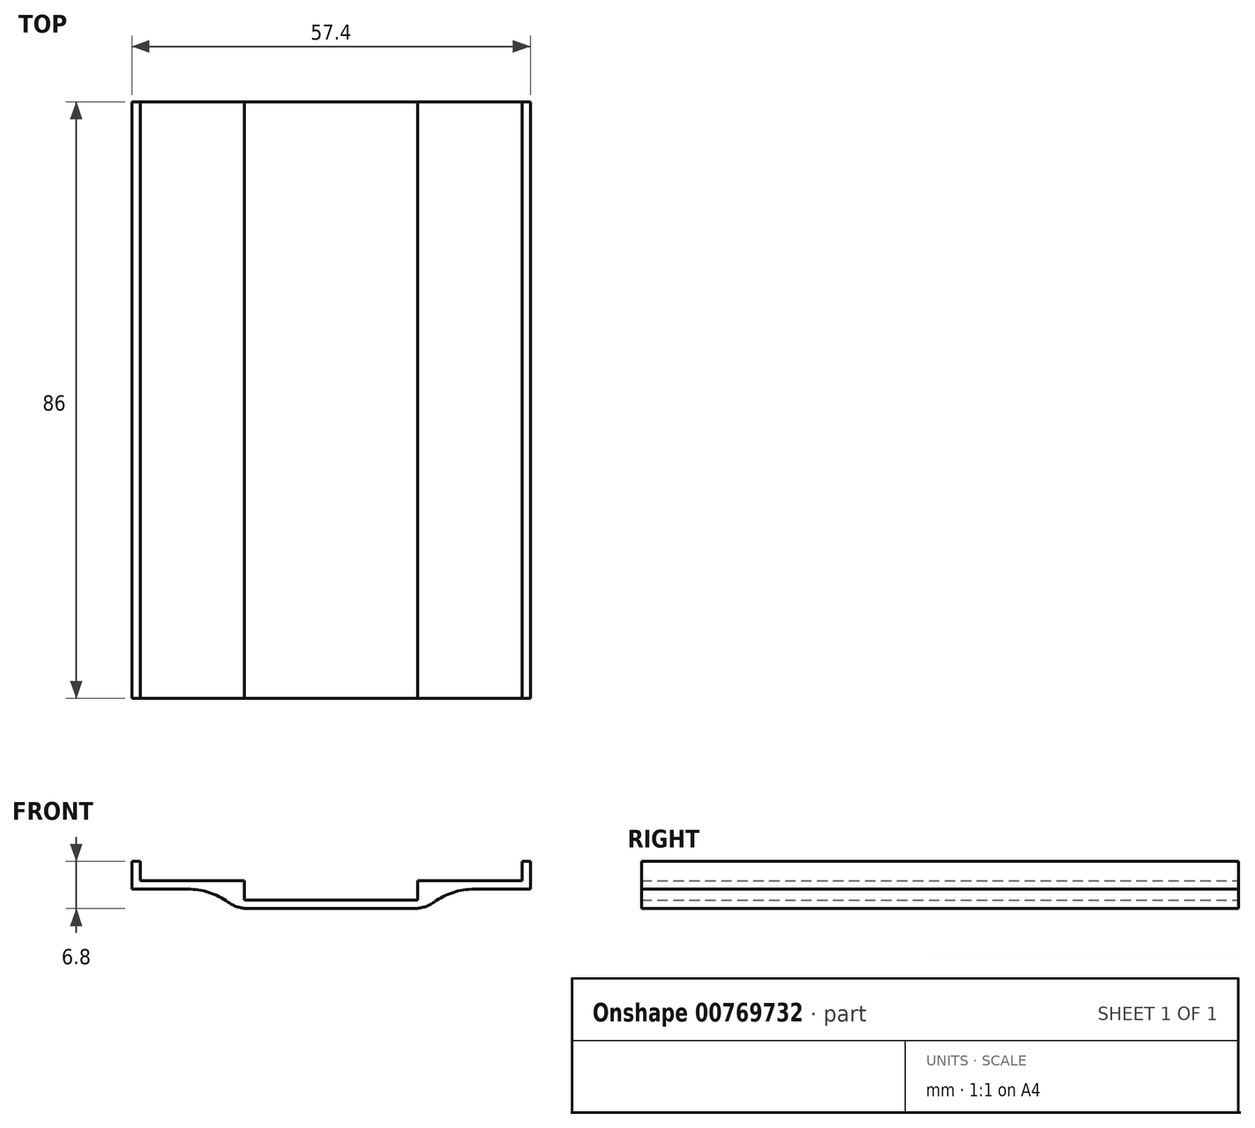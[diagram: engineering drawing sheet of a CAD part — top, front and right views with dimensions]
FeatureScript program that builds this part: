
annotation { "Feature Type Name" : "Feature", "Feature Type Description" : "" }
export const myFeature = defineFeature(function(context is Context, id is Id, definition is map)
    precondition{}
    {
        {
            var Q0;
            Q0=qCreatedBy(makeId("Front.planeOp"),FACE);
            var sketch = newSketch(context, id + "F0", { "sketchPlane" : qUnion([Q0])});
            skLineSegment(sketch, "E0.bottom", {"start": v(-27.5, 2.8) * mm, "end": v(-12.5, 2.8) * mm});
            skLineSegment(sketch, "E0.top", {"start": v(-27.5, 5.6) * mm, "end": v(27.5, 5.6) * mm});
            skLineSegment(sketch, "E0.left", {"start": v(-27.5, 2.8) * mm, "end": v(-27.5, 5.6) * mm});
            skLineSegment(sketch, "E0.right", {"start": v(27.5, 2.8) * mm, "end": v(27.5, 5.6) * mm});
            skLineSegment(sketch, "E1.top", {"start": v(-12.5, 0) * mm, "end": v(12.5, 0) * mm});
            skLineSegment(sketch, "E1.left", {"start": v(-12.5, 2.8) * mm, "end": v(-12.5, 0) * mm});
            skLineSegment(sketch, "E1.right", {"start": v(12.5, 2.8) * mm, "end": v(12.5, 0) * mm});
            skLineSegment(sketch, "E2.trimOffspring", {"start": v(12.5, 2.8) * mm, "end": v(27.5, 2.8) * mm});
            skSolve(sketch);
        }
        {
            var Q0;
            Q0 = qSketchRegion(id + "F0", true);
            extrude(context, id + "F1", {"entities" : qUnion([Q0]), "depth" : 86 * mm, "offsetDistance" : 25 * mm});
        }
        {
            var Q0;
            Q0=makeQuery(id+"F1.opExtrude","SWEPT_FACE",FACE,{"disambiguationData":[OSD([sQuery(id+"F0.wireOp",EDGE,"E0.top")])]});
            var Q1;
            Q1=makeQuery(id+"F1.opExtrude","CAP_FACE",FACE,{"disambiguationData":[OSD([sQuery(id+"F0.wireOp",EDGE,"E0.bottom"),sQuery(id+"F0.wireOp",EDGE,"E0.top"),sQuery(id+"F0.wireOp",EDGE,"E0.left"),sQuery(id+"F0.wireOp",EDGE,"E0.right"),sQuery(id+"F0.wireOp",EDGE,"E1.top"),sQuery(id+"F0.wireOp",EDGE,"E1.left"),sQuery(id+"F0.wireOp",EDGE,"E1.right"),sQuery(id+"F0.wireOp",EDGE,"E2.trimOffspring")])],"isStart":false});
            var Q2;
            Q2=makeQuery(id+"F1.opExtrude","CAP_FACE",FACE,{"disambiguationData":[OSD([sQuery(id+"F0.wireOp",EDGE,"E0.bottom"),sQuery(id+"F0.wireOp",EDGE,"E0.top"),sQuery(id+"F0.wireOp",EDGE,"E0.left"),sQuery(id+"F0.wireOp",EDGE,"E0.right"),sQuery(id+"F0.wireOp",EDGE,"E1.top"),sQuery(id+"F0.wireOp",EDGE,"E1.left"),sQuery(id+"F0.wireOp",EDGE,"E1.right"),sQuery(id+"F0.wireOp",EDGE,"E2.trimOffspring")])],"isStart":true});
            shell(context, id + "F2", {"entities" : qUnion([Q0, Q1, Q2]), "thickness" : 1.2 * mm, "oppositeDirection" : true});
        }
        {
            var Q0;
            Q0=makeQuery(id+"F1.opExtrude","SWEPT_EDGE",EDGE,{"disambiguationData":[OSD([sQuery(id+"F0.wireOp",EDGE,"E0.bottom"),sQuery(id+"F0.wireOp",EDGE,"E1.left")])]});
            var Q1;
            Q1=makeQuery(id+"F1.opExtrude","SWEPT_EDGE",EDGE,{"disambiguationData":[OSD([sQuery(id+"F0.wireOp",EDGE,"E1.right"),sQuery(id+"F0.wireOp",EDGE,"E2.trimOffspring")])]});
            fillet(context, id + "F3", {"entities" : qUnion([Q0, Q1]), "radius" : 10 * mm, "tangentPropagation" : true, "allowEdgeOverflow" : false});
        }
        {
            var Q0;
            Q0=makeQuery(id+"F3.opFillet","BLEND_EDGE",EDGE,{"blendedFrom":[makeQuery(id+"F1.opExtrude","SWEPT_EDGE",EDGE,{"disambiguationData":[OSD([sQuery(id+"F0.wireOp",EDGE,"E0.bottom"),sQuery(id+"F0.wireOp",EDGE,"E1.left")])]}),makeQuery(id+"F1.opExtrude","SWEPT_FACE",FACE,{"disambiguationData":[OSD([sQuery(id+"F0.wireOp",EDGE,"E1.top")])]})],"blendedInto":[makeQuery(id+"F1.opExtrude","SWEPT_FACE",FACE,{"disambiguationData":[OSD([sQuery(id+"F0.wireOp",EDGE,"E1.top")])]})]});
            var Q1;
            Q1=makeQuery(id+"F3.opFillet","BLEND_EDGE",EDGE,{"blendedFrom":[makeQuery(id+"F1.opExtrude","SWEPT_EDGE",EDGE,{"disambiguationData":[OSD([sQuery(id+"F0.wireOp",EDGE,"E1.right"),sQuery(id+"F0.wireOp",EDGE,"E2.trimOffspring")])]}),makeQuery(id+"F1.opExtrude","SWEPT_FACE",FACE,{"disambiguationData":[OSD([sQuery(id+"F0.wireOp",EDGE,"E1.top")])]})],"blendedInto":[makeQuery(id+"F1.opExtrude","SWEPT_FACE",FACE,{"disambiguationData":[OSD([sQuery(id+"F0.wireOp",EDGE,"E1.top")])]})]});
            fillet(context, id + "F4", {"entities" : qUnion([Q0, Q1]), "radius" : 5 * mm, "tangentPropagation" : true, "allowEdgeOverflow" : false});
        }
    });
